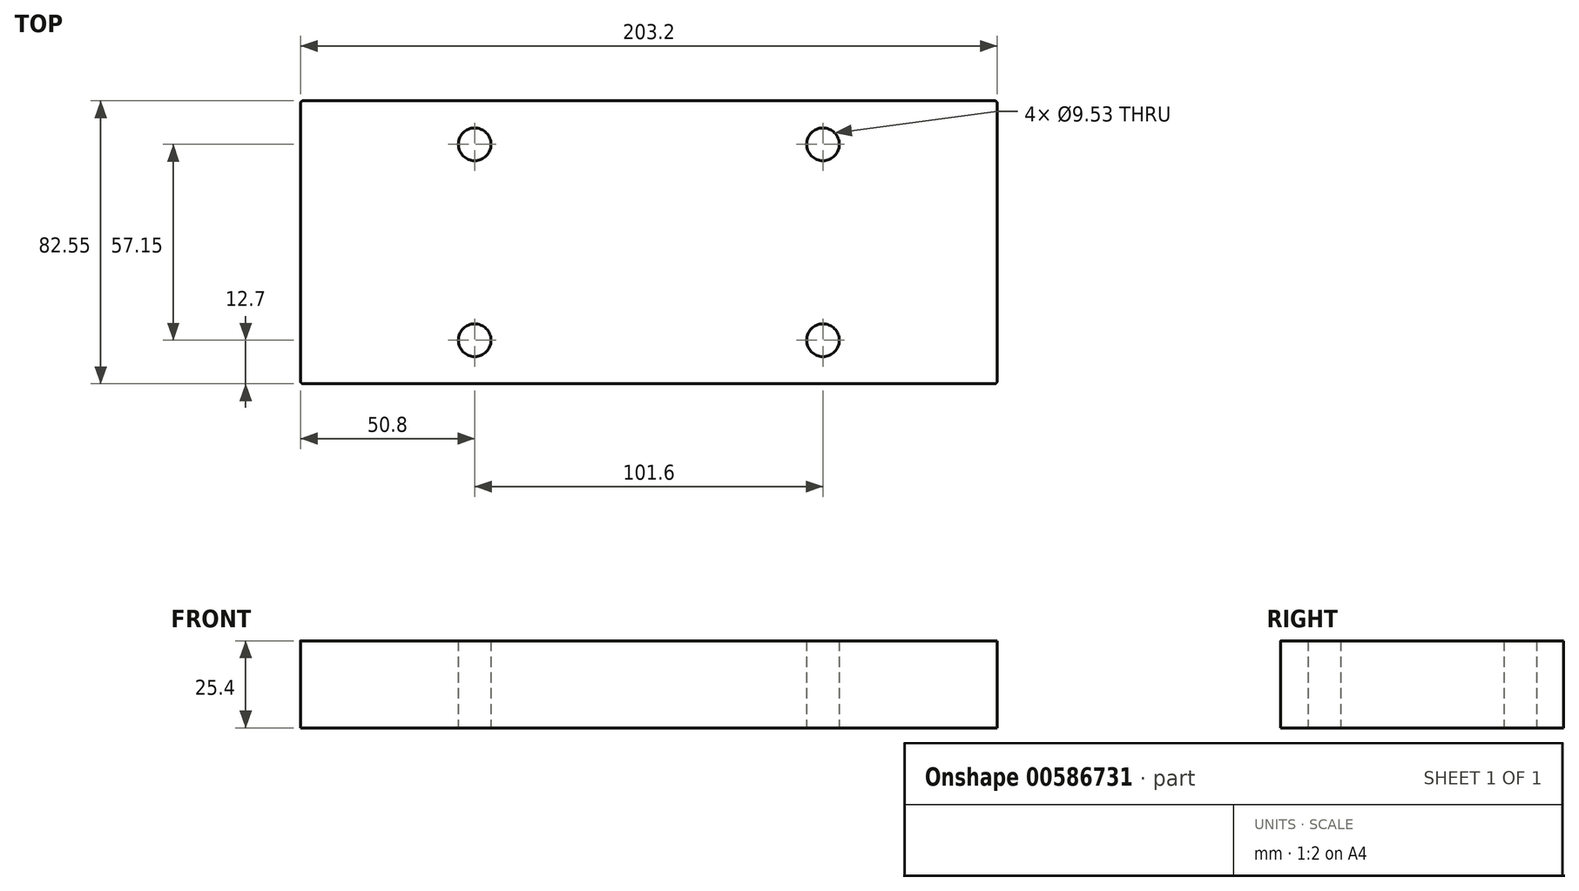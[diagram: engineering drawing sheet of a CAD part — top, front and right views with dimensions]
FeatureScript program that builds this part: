
annotation { "Feature Type Name" : "Feature", "Feature Type Description" : "" }
export const myFeature = defineFeature(function(context is Context, id is Id, definition is map)
    precondition{}
    {
        {
            var Q0;
            Q0=qCreatedBy(makeId("Top.planeOp"),FACE);
            var sketch = newSketch(context, id + "F0", { "sketchPlane" : qUnion([Q0])});
            skLineSegment(sketch, "E0.bottom", {"start": v(-50.04, 12.7) * mm, "end": v(151.64, 12.7) * mm});
            skLineSegment(sketch, "E0.top", {"start": v(-50.04, -69.85) * mm, "end": v(151.64, -69.85) * mm});
            skLineSegment(sketch, "E0.left", {"start": v(-50.8, 11.94) * mm, "end": v(-50.8, -69.09) * mm});
            skLineSegment(sketch, "E0.right", {"start": v(152.4, 11.94) * mm, "end": v(152.4, -69.09) * mm});
            skCircle(sketch, "E1", {"center": v(0, -57.15) * mm, "radius": 4.76 * mm});
            skCircle(sketch, "E2", {"center": v(0, 0) * mm, "radius": 4.76 * mm});
            skCircle(sketch, "E3", {"center": v(101.6, 0) * mm, "radius": 4.76 * mm});
            skCircle(sketch, "E4", {"center": v(101.6, -57.15) * mm, "radius": 4.76 * mm});
            skLineSegment(sketch, "E5.bottom", {"start": v(0, -57.15) * mm, "end": v(101.6, -57.15) * mm, "construction": true});
            skLineSegment(sketch, "E5.top", {"start": v(0, 0) * mm, "end": v(101.6, 0) * mm, "construction": true});
            skLineSegment(sketch, "E5.left", {"start": v(0, -57.15) * mm, "end": v(0, 0) * mm, "construction": true});
            skLineSegment(sketch, "E5.right", {"start": v(101.6, -57.15) * mm, "end": v(101.6, 0) * mm, "construction": true});
            skPoint(sketch, "E6.visualSharp", {"position": v(-50.8, 12.7) * mm});
            skArc(sketch, "E6.filletArc", {"start": v(-50.04, 12.7) * mm, "mid": v(-50.58, 12.48) * mm, "end": v(-50.8, 11.94) * mm});
            skPoint(sketch, "E7.visualSharp", {"position": v(-50.8, -69.85) * mm});
            skArc(sketch, "E7.filletArc", {"start": v(-50.8, -69.09) * mm, "mid": v(-50.58, -69.63) * mm, "end": v(-50.04, -69.85) * mm});
            skPoint(sketch, "E8.visualSharp", {"position": v(152.4, 12.7) * mm});
            skArc(sketch, "E8.filletArc", {"start": v(152.4, 11.94) * mm, "mid": v(152.18, 12.48) * mm, "end": v(151.64, 12.7) * mm});
            skPoint(sketch, "E9.visualSharp", {"position": v(152.4, -69.85) * mm});
            skArc(sketch, "E9.filletArc", {"start": v(151.64, -69.85) * mm, "mid": v(152.18, -69.63) * mm, "end": v(152.4, -69.09) * mm});
            skSolve(sketch);
        }
        {
            var Q0;
            Q0 = qSketchRegion(id + "F0", true);
            extrude(context, id + "F1", {"entities" : qUnion([Q0]), "depth" : 25.4 * mm, "offsetDistance" : 25.4 * mm});
        }
    });
